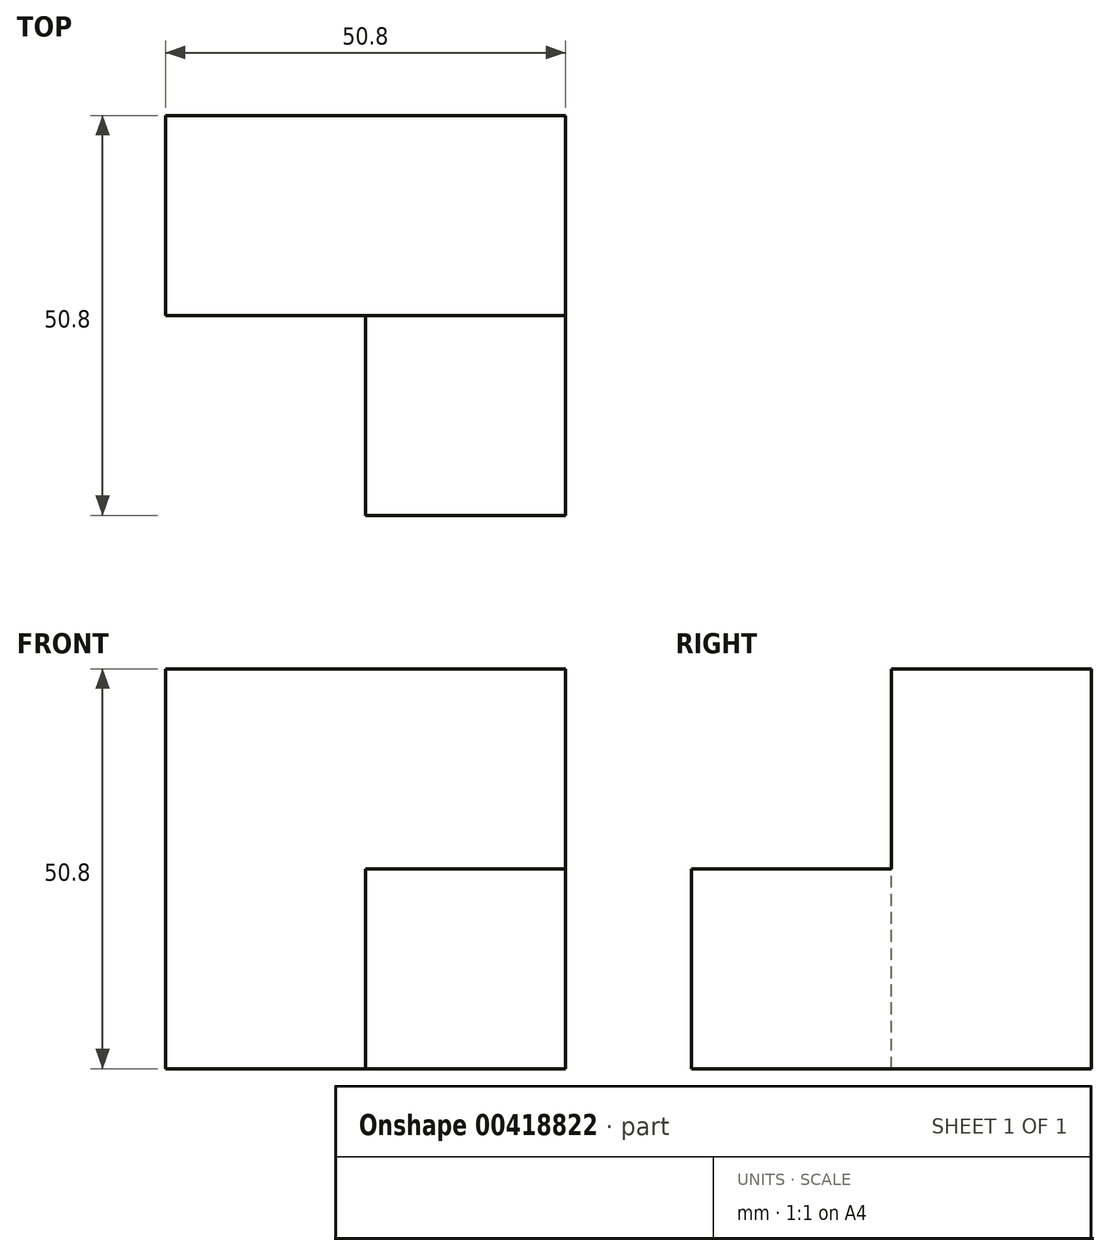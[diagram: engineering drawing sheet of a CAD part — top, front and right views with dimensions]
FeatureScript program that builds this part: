
annotation { "Feature Type Name" : "Feature", "Feature Type Description" : "" }
export const myFeature = defineFeature(function(context is Context, id is Id, definition is map)
    precondition{}
    {
        {
            var Q0;
            Q0=qCreatedBy(makeId("Front.planeOp"),FACE);
            var sketch = newSketch(context, id + "F0", { "sketchPlane" : qUnion([Q0])});
            skLineSegment(sketch, "E0.bottom", {"start": v(0, 0) * mm, "end": v(-50.8, 0) * mm});
            skLineSegment(sketch, "E0.top", {"start": v(0, 50.8) * mm, "end": v(-50.8, 50.8) * mm});
            skLineSegment(sketch, "E0.left", {"start": v(0, 0) * mm, "end": v(0, 50.8) * mm});
            skLineSegment(sketch, "E0.right", {"start": v(-50.8, 0) * mm, "end": v(-50.8, 50.8) * mm});
            skSolve(sketch);
        }
        {
            var Q0;
            Q0=makeQuery(id+"F0.imprint","IMPRINT",FACE,{"disambiguationData":[TD([[makeQuery(id+"F0.imprint","IMPRINT",EDGE,{"derivedFrom":sQuery(id+"F0.wireOp",EDGE,"E0.bottom")}),-1.0]])]});
            var sketch = newSketch(context, id + "F1", { "sketchPlane" : qUnion([Q0])});
            skLineSegment(sketch, "E1.bottom", {"start": v(0, 0) * mm, "end": v(-25.4, 0) * mm});
            skLineSegment(sketch, "E1.top", {"start": v(0, 25.4) * mm, "end": v(-25.4, 25.4) * mm});
            skLineSegment(sketch, "E1.left", {"start": v(0, 0) * mm, "end": v(0, 25.4) * mm});
            skLineSegment(sketch, "E1.right", {"start": v(-25.4, 0) * mm, "end": v(-25.4, 25.4) * mm});
            skSolve(sketch);
        }
        {
            var Q0;
            Q0 = qSketchRegion(id + "F1", true);
            extrude(context, id + "F2", {"entities" : qUnion([Q0]), "depth" : 50.8 * mm});
        }
        {
            var Q0;
            Q0 = qSketchRegion(id + "F0", true);
            extrude(context, id + "F3", {"entities" : qUnion([Q0]), "operationType" : NewBodyOperationType.ADD, "depth" : 25.4 * mm});
        }
        {
            var Q0;
            Q0 = qSketchRegion(id + "F0", true);
            var Q1;
            Q1=makeQuery(id+"F0.imprint","IMPRINT",FACE,{"disambiguationData":[TD([[makeQuery(id+"F0.imprint","IMPRINT",EDGE,{"derivedFrom":sQuery(id+"F0.wireOp",EDGE,"E0.bottom")}),-1.0]])]});
            extrude(context, id + "F4", {"entities" : qUnion([Q0, Q1]), "operationType" : NewBodyOperationType.ADD, "depth" : 25.4 * mm});
        }
    });
